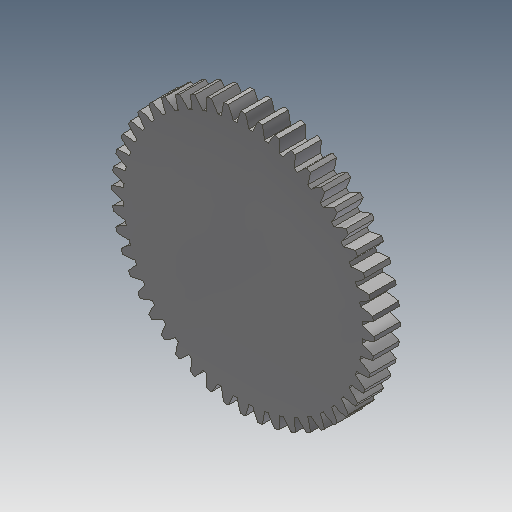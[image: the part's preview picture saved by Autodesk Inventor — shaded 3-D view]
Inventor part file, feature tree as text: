
AUTODESK INVENTOR PART (.ipt)
format: ipt  version: 2017 (Build 210142000, 142)  size: 321,536 bytes
history: native  units: mm (DEFAULTED — no unit token found)
features: plane x3, other x3, sketch x2, extrude x1
ambient origin geometry x8: Origin, YZ Plane, XZ Plane, XY Plane, X Axis, Y Axis, Z Axis, Center Point
bodies: Solid1 (feature_tree)
feature tree (9):
  extrude  "Extrusion1"  Depth=1.0mm TaperAngle=0.0deg
  plane  "Work Plane2"
  plane  "Work Plane8"
  plane  "Work Plane9"
  other  "Цилиндрическое зубчатое зацепление"
  sketch  "Sketch1"  dims[d0=10.078425mm d1=1.0mm d2=0.0mm]
  sketch  "Sketch2"  dims[d3=9.678972mm d4=10.0mm d5=0.0mm d16=5.948535mm d17=0.0mm d34=0.654498mm d39=0.0mm d41=0.0mm d43=5.948535mm d46=5.948535mm d47=0.0mm d48=0.0mm]
  other  "Srf1"
  other  "Средний диаметр"
